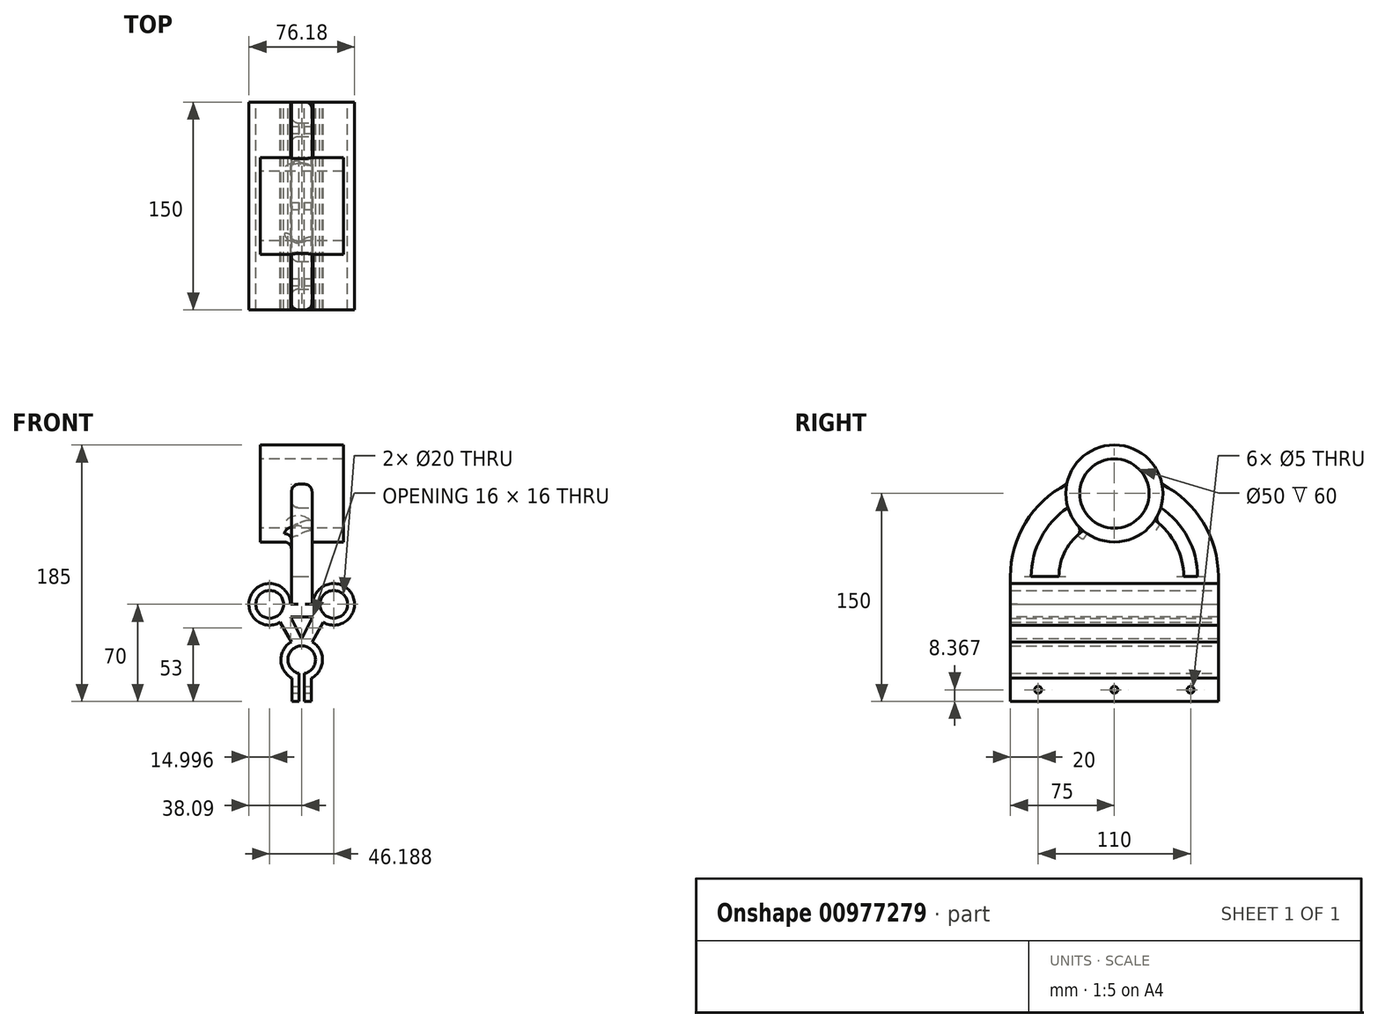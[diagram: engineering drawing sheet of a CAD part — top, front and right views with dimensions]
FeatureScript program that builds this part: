
annotation { "Feature Type Name" : "Feature", "Feature Type Description" : "" }
export const myFeature = defineFeature(function(context is Context, id is Id, definition is map)
    precondition{}
    {
        {
            var Q0;
            Q0=qCreatedBy(makeId("Front.planeOp"),FACE);
            var sketch = newSketch(context, id + "F0", { "sketchPlane" : qUnion([Q0])});
            skCircle(sketch, "E0", {"center": v(0, 0) * mm, "radius": 10 * mm});
            skCircle(sketch, "E1", {"center": v(23.1, 40) * mm, "radius": 10 * mm});
            skCircle(sketch, "E2", {"center": v(-23.1, 40) * mm, "radius": 10 * mm});
            skCircle(sketch, "E3", {"center": v(-23.1, 40) * mm, "radius": 15 * mm});
            skCircle(sketch, "E4", {"center": v(23.1, 40) * mm, "radius": 15 * mm});
            skCircle(sketch, "E5", {"center": v(0, 0) * mm, "radius": 15 * mm});
            skLineSegment(sketch, "E6", {"start": v(0, 0) * mm, "end": v(-23.1, 40) * mm});
            skLineSegment(sketch, "E7", {"start": v(23.1, 40) * mm, "end": v(0, 0) * mm});
            skLineSegment(sketch, "E8", {"start": v(-23.1, 40) * mm, "end": v(23.1, 40) * mm});
            skLineSegment(sketch, "E9.bottom", {"start": v(-2, 0) * mm, "end": v(2, 0) * mm});
            skLineSegment(sketch, "E9.top", {"start": v(-2, -30) * mm, "end": v(2, -30) * mm});
            skLineSegment(sketch, "E9.left", {"start": v(-2, 0) * mm, "end": v(-2, -30) * mm});
            skLineSegment(sketch, "E9.right", {"start": v(2, 0) * mm, "end": v(2, -30) * mm});
            skPoint(sketch, "E9.middle", {"position": v(0, -15) * mm});
            skLineSegment(sketch, "E10.bottom", {"start": v(7, -30) * mm, "end": v(-7, -30) * mm});
            skLineSegment(sketch, "E10.top", {"start": v(7, 0) * mm, "end": v(-7, 0) * mm});
            skLineSegment(sketch, "E10.left", {"start": v(7, -30) * mm, "end": v(7, 0) * mm});
            skLineSegment(sketch, "E10.right", {"start": v(-7, -30) * mm, "end": v(-7, 0) * mm});
            skLineSegment(sketch, "E11.bottom", {"start": v(-7.5, 60) * mm, "end": v(7.5, 60) * mm});
            skLineSegment(sketch, "E11.top", {"start": v(-7.5, 20) * mm, "end": v(7.5, 20) * mm});
            skLineSegment(sketch, "E11.left", {"start": v(-7.5, 60) * mm, "end": v(-7.5, 20) * mm});
            skLineSegment(sketch, "E11.right", {"start": v(7.5, 60) * mm, "end": v(7.5, 20) * mm});
            skPoint(sketch, "E11.middle", {"position": v(0, 40) * mm});
            skSolve(sketch);
        }
        {
            var Q0;
            {var subQ5=sQuery(id+"F0.wireOp",EDGE,"E11.bottom");Q0=makeQuery(id+"F0.imprint","IMPRINT",FACE,{"disambiguationData":[TD([[makeQuery(id+"F0.imprint","IMPRINT",EDGE,{"derivedFrom":subQ5}),-1.0]])]});}
            var Q1;
            {var subQ0=sQuery(id+"F0.wireOp",EDGE,"E7");var subQ1=sQuery(id+"F0.wireOp",EDGE,"E1");var subQ2=makeQuery(id+"F0.imprint","INTERSECT",VERTEX,{"derivedFrom":[subQ1,subQ0]});Q1=makeQuery(id+"F0.imprint","IMPRINT",FACE,{"disambiguationData":[TD([[makeQuery(id+"F0.imprint","IMPRINT",EDGE,{"disambiguationData":[TD([[subQ2,-1.0]])],"derivedFrom":subQ1}),-1.0]])]});}
            var Q2;
            {var subQ0=sQuery(id+"F0.wireOp",EDGE,"E6");var subQ1=sQuery(id+"F0.wireOp",EDGE,"E2");var subQ2=makeQuery(id+"F0.imprint","INTERSECT",VERTEX,{"derivedFrom":[subQ1,subQ0]});Q2=makeQuery(id+"F0.imprint","IMPRINT",FACE,{"disambiguationData":[TD([[makeQuery(id+"F0.imprint","IMPRINT",EDGE,{"disambiguationData":[TD([[subQ2,1.0]])],"derivedFrom":subQ1}),-1.0]])]});}
            var Q3;
            {var subQ0=sQuery(id+"F0.wireOp",EDGE,"E10.right");var subQ1=sQuery(id+"F0.wireOp",EDGE,"E5");var subQ2=makeQuery(id+"F0.imprint","INTERSECT",VERTEX,{"derivedFrom":[subQ1,subQ0]});Q3=makeQuery(id+"F0.imprint","IMPRINT",FACE,{"disambiguationData":[TD([[makeQuery(id+"F0.imprint","IMPRINT",EDGE,{"disambiguationData":[TD([[subQ2,-1.0]])],"derivedFrom":subQ1}),-1.0]])]});}
            var Q4;
            {var subQ0=sQuery(id+"F0.wireOp",EDGE,"E10.left");var subQ1=sQuery(id+"F0.wireOp",EDGE,"E5");var subQ2=makeQuery(id+"F0.imprint","INTERSECT",VERTEX,{"derivedFrom":[subQ1,subQ0]});Q4=makeQuery(id+"F0.imprint","IMPRINT",FACE,{"disambiguationData":[TD([[makeQuery(id+"F0.imprint","IMPRINT",EDGE,{"disambiguationData":[TD([[subQ2,1.0]])],"derivedFrom":subQ1}),-1.0]])]});}
            var Q5;
            {var subQ5=sQuery(id+"F0.wireOp",EDGE,"E11.top");Q5=makeQuery(id+"F0.imprint","IMPRINT",FACE,{"disambiguationData":[TD([[makeQuery(id+"F0.imprint","IMPRINT",EDGE,{"derivedFrom":subQ5}),1.0]])]});}
            var Q6;
            {var subQ0=sQuery(id+"F0.wireOp",EDGE,"E6");var subQ1=sQuery(id+"F0.wireOp",EDGE,"E0");var subQ2=makeQuery(id+"F0.imprint","INTERSECT",VERTEX,{"derivedFrom":[subQ1,subQ0]});Q6=makeQuery(id+"F0.imprint","IMPRINT",FACE,{"disambiguationData":[TD([[makeQuery(id+"F0.imprint","IMPRINT",EDGE,{"disambiguationData":[TD([[subQ2,-1.0]])],"derivedFrom":subQ1}),-1.0]])]});}
            var Q7;
            {var subQ0=sQuery(id+"F0.wireOp",EDGE,"E7");var subQ1=sQuery(id+"F0.wireOp",EDGE,"E0");var subQ2=makeQuery(id+"F0.imprint","INTERSECT",VERTEX,{"derivedFrom":[subQ1,subQ0]});Q7=makeQuery(id+"F0.imprint","IMPRINT",FACE,{"disambiguationData":[TD([[makeQuery(id+"F0.imprint","IMPRINT",EDGE,{"disambiguationData":[TD([[subQ2,1.0]])],"derivedFrom":subQ1}),-1.0]])]});}
            var Q8;
            {var subQ0=sQuery(id+"F0.wireOp",EDGE,"E7");var subQ1=sQuery(id+"F0.wireOp",EDGE,"E1");var subQ2=makeQuery(id+"F0.imprint","INTERSECT",VERTEX,{"derivedFrom":[subQ1,subQ0]});Q8=makeQuery(id+"F0.imprint","IMPRINT",FACE,{"disambiguationData":[TD([[makeQuery(id+"F0.imprint","IMPRINT",EDGE,{"disambiguationData":[TD([[subQ2,1.0]])],"derivedFrom":subQ1}),-1.0]])]});}
            var Q9;
            {var subQ0=sQuery(id+"F0.wireOp",EDGE,"E6");var subQ1=sQuery(id+"F0.wireOp",EDGE,"E2");var subQ2=makeQuery(id+"F0.imprint","INTERSECT",VERTEX,{"derivedFrom":[subQ1,subQ0]});Q9=makeQuery(id+"F0.imprint","IMPRINT",FACE,{"disambiguationData":[TD([[makeQuery(id+"F0.imprint","IMPRINT",EDGE,{"disambiguationData":[TD([[subQ2,-1.0]])],"derivedFrom":subQ1}),-1.0]])]});}
            var Q10;
            {var subQ0=sQuery(id+"F0.wireOp",EDGE,"E6");var subQ1=sQuery(id+"F0.wireOp",EDGE,"E0");var subQ2=makeQuery(id+"F0.imprint","INTERSECT",VERTEX,{"derivedFrom":[subQ1,subQ0]});Q10=makeQuery(id+"F0.imprint","IMPRINT",FACE,{"disambiguationData":[TD([[makeQuery(id+"F0.imprint","IMPRINT",EDGE,{"disambiguationData":[TD([[subQ2,1.0]])],"derivedFrom":subQ1}),-1.0]])]});}
            var Q11;
            {var subQ0=sQuery(id+"F0.wireOp",EDGE,"E10.right");var subQ1=sQuery(id+"F0.wireOp",EDGE,"E0");var subQ2=makeQuery(id+"F0.imprint","INTERSECT",VERTEX,{"derivedFrom":[subQ1,subQ0]});Q11=makeQuery(id+"F0.imprint","IMPRINT",FACE,{"disambiguationData":[TD([[makeQuery(id+"F0.imprint","IMPRINT",EDGE,{"disambiguationData":[TD([[subQ2,-1.0]])],"derivedFrom":subQ1}),-1.0]])]});}
            var Q12;
            {var subQ0=sQuery(id+"F0.wireOp",EDGE,"E9.right");var subQ1=sQuery(id+"F0.wireOp",EDGE,"E0");var subQ2=makeQuery(id+"F0.imprint","INTERSECT",VERTEX,{"derivedFrom":[subQ1,subQ0]});Q12=makeQuery(id+"F0.imprint","IMPRINT",FACE,{"disambiguationData":[TD([[makeQuery(id+"F0.imprint","IMPRINT",EDGE,{"disambiguationData":[TD([[subQ2,-1.0]])],"derivedFrom":subQ1}),-1.0]])]});}
            var Q13;
            {var subQ16=sQuery(id+"F0.wireOp",EDGE,"E11.top");Q13=makeQuery(id+"F0.imprint","IMPRINT",FACE,{"disambiguationData":[TD([[makeQuery(id+"F0.imprint","IMPRINT",EDGE,{"derivedFrom":subQ16}),-1.0]])]});}
            extrude(context, id + "F1", {"entities" : qUnion([Q0, Q1, Q2, Q3, Q4, Q5, Q6, Q7, Q8, Q9, Q10, Q11, Q12, Q13]), "depth" : 150 * mm, "offsetDistance" : 25 * mm});
        }
        {
            var Q0;
            Q0=makeQuery(id+"F1.opExtrude","SWEPT_FACE",FACE,{"disambiguationData":[OSD([sQuery(id+"F0.wireOp",EDGE,"E10.left")])]});
            var sketch = newSketch(context, id + "F2", { "sketchPlane" : qUnion([Q0])});
            skCircle(sketch, "E12", {"center": v(-130, -21.63) * mm, "radius": 2.5 * mm});
            skPoint(sketch, "E12.centerSnap0", {"position": v(-150, -21.63) * mm});
            skCircle(sketch, "E13", {"center": v(-75, -21.63) * mm, "radius": 2.5 * mm});
            skPoint(sketch, "E13.centerSnap0", {"position": v(-75, -30) * mm});
            skCircle(sketch, "E14", {"center": v(-20, -21.63) * mm, "radius": 2.5 * mm});
            skPoint(sketch, "E14.centerSnap0", {"position": v(0, -21.63) * mm});
            skSolve(sketch);
        }
        {
            var Q0;
            Q0=qSketchRegion(id+"F2",true);
            extrude(context, id + "F3", {"entities" : qUnion([Q0]), "operationType" : NewBodyOperationType.REMOVE, "oppositeDirection" : true, "depth" : 25 * mm, "offsetDistance" : 25 * mm});
        }
        {
            var Q0;
            Q0=qCreatedBy(makeId("Right.planeOp"),FACE);
            var sketch = newSketch(context, id + "F4", { "sketchPlane" : qUnion([Q0])});
            skArc(sketch, "E15", {"start": v(0, 60) * mm, "mid": v(-75, 135) * mm, "end": v(-150, 60) * mm});
            skCircle(sketch, "E16", {"center": v(-75, 120) * mm, "radius": 25 * mm});
            skCircle(sketch, "E17", {"center": v(-75, 120) * mm, "radius": 35 * mm});
            skLineSegment(sketch, "E18", {"start": v(0, 60) * mm, "end": v(-150, 60) * mm});
            skSolve(sketch);
        }
        {
            var Q0;
            Q0=qSketchRegion(id+"F4",true);
            var Q1;
            Q1=makeQuery(id+"F4.imprint","IMPRINT",FACE,{"disambiguationData":[TD([[makeQuery(id+"F4.imprint","IMPRINT",EDGE,{"derivedFrom":sQuery(id+"F4.wireOp",EDGE,"E16")}),-1.0]])]});
            extrude(context, id + "F5", {"entities" : qUnion([Q0, Q1]), "operationType" : NewBodyOperationType.ADD, "depth" : 15 * mm, "offsetDistance" : 25 * mm, "symmetric" : true});
        }
        {
            var Q0;
            Q0=makeQuery(id+"F4.imprint","IMPRINT",FACE,{"disambiguationData":[TD([[makeQuery(id+"F4.imprint","IMPRINT",EDGE,{"derivedFrom":sQuery(id+"F4.wireOp",EDGE,"E16")}),-1.0]])]});
            extrude(context, id + "F6", {"entities" : qUnion([Q0]), "operationType" : NewBodyOperationType.ADD, "depth" : 60 * mm, "offsetDistance" : 25 * mm, "symmetric" : true});
        }
        {
            var Q0;
            Q0=makeQuery(id+"F5.boolean.opBoolean","MERGE",FACE,{"derivedFrom":[makeQuery(id+"F1.opExtrude","SWEPT_FACE",FACE,{"disambiguationData":[OSD([sQuery(id+"F0.wireOp",EDGE,"E11.right")])]}),makeQuery(id+"F5.opExtrude","CAP_FACE",FACE,{"disambiguationData":[OSD([sQuery(id+"F4.wireOp",EDGE,"E15"),sQuery(id+"F4.wireOp",EDGE,"E16"),sQuery(id+"F4.wireOp",EDGE,"E18")])],"isStart":false})]});
            var sketch = newSketch(context, id + "F7", { "sketchPlane" : qUnion([Q0])});
            skCircle(sketch, "E19", {"center": v(-75, 60) * mm, "radius": 60 * mm});
            skCircle(sketch, "E20", {"center": v(-75, 60) * mm, "radius": 40 * mm});
            skLineSegment(sketch, "E21", {"start": v(-150, 60) * mm, "end": v(0, 60) * mm});
            skCircle(sketch, "E22", {"center": v(-75, 60) * mm, "radius": 50 * mm});
            skSolve(sketch);
        }
        {
            var Q0;
            {var subQ0=sQuery(id+"F7.wireOp",EDGE,"E21");var subQ1=sQuery(id+"F7.wireOp",EDGE,"E19");var subQ2=makeQuery(id+"F7.imprint","INTERSECT",VERTEX,{"disambiguationData":[OD(0.0)],"derivedFrom":[subQ1,subQ0]});Q0=makeQuery(id+"F7.imprint","IMPRINT",FACE,{"disambiguationData":[TD([[makeQuery(id+"F7.imprint","IMPRINT",EDGE,{"disambiguationData":[TD([[subQ2,1.0]])],"derivedFrom":subQ0}),1.0]])]});}
            var Q1;
            {var subQ0=sQuery(id+"F7.wireOp",EDGE,"E21");var subQ1=sQuery(id+"F7.wireOp",EDGE,"E19");var subQ2=makeQuery(id+"F7.imprint","INTERSECT",VERTEX,{"disambiguationData":[OD(1.0)],"derivedFrom":[subQ1,subQ0]});Q1=makeQuery(id+"F7.imprint","IMPRINT",FACE,{"disambiguationData":[TD([[makeQuery(id+"F7.imprint","IMPRINT",EDGE,{"disambiguationData":[TD([[subQ2,-1.0]])],"derivedFrom":subQ0}),1.0]])]});}
            var Q2;
            {var subQ0=sQuery(id+"F7.wireOp",EDGE,"E21");var subQ1=sQuery(id+"F7.wireOp",EDGE,"E20");var subQ2=makeQuery(id+"F7.imprint","INTERSECT",VERTEX,{"disambiguationData":[OD(0.0)],"derivedFrom":[subQ1,subQ0]});Q2=makeQuery(id+"F7.imprint","IMPRINT",FACE,{"disambiguationData":[TD([[makeQuery(id+"F7.imprint","IMPRINT",EDGE,{"disambiguationData":[TD([[subQ2,1.0]])],"derivedFrom":subQ0}),1.0]])]});}
            extrude(context, id + "F8", {"entities" : qUnion([Q0, Q1, Q2]), "operationType" : NewBodyOperationType.REMOVE, "oppositeDirection" : true, "depth" : 25 * mm, "offsetDistance" : 25 * mm});
        }
        {
            var Q0;
            Q0=makeQuery(id+"F1.opExtrude","CAP_FACE",FACE,{"disambiguationData":[OSD([sQuery(id+"F0.wireOp",EDGE,"E0"),sQuery(id+"F0.wireOp",EDGE,"E1"),sQuery(id+"F0.wireOp",EDGE,"E2"),sQuery(id+"F0.wireOp",EDGE,"E3"),sQuery(id+"F0.wireOp",EDGE,"E4"),sQuery(id+"F0.wireOp",EDGE,"E5"),sQuery(id+"F0.wireOp",EDGE,"E6"),sQuery(id+"F0.wireOp",EDGE,"E7"),sQuery(id+"F0.wireOp",EDGE,"E8"),sQuery(id+"F0.wireOp",EDGE,"E9.left"),sQuery(id+"F0.wireOp",EDGE,"E9.right"),sQuery(id+"F0.wireOp",EDGE,"E10.bottom"),sQuery(id+"F0.wireOp",EDGE,"E10.left"),sQuery(id+"F0.wireOp",EDGE,"E10.right"),sQuery(id+"F0.wireOp",EDGE,"E11.bottom"),sQuery(id+"F0.wireOp",EDGE,"E11.left"),sQuery(id+"F0.wireOp",EDGE,"E11.right")])],"isStart":false});
            var sketch = newSketch(context, id + "F9", { "sketchPlane" : qUnion([Q0])});
            skLineSegment(sketch, "E23", {"start": v(0, 15) * mm, "end": v(8, 31) * mm});
            skLineSegment(sketch, "E24", {"start": v(8, 31) * mm, "end": v(-8, 31) * mm});
            skLineSegment(sketch, "E25", {"start": v(-8, 31) * mm, "end": v(0, 15) * mm});
            skSolve(sketch);
        }
        {
            var Q0;
            Q0=makeQuery(id+"F9.imprint","IMPRINT",FACE,{"disambiguationData":[TD([[makeQuery(id+"F9.imprint","IMPRINT",EDGE,{"derivedFrom":sQuery(id+"F9.wireOp",EDGE,"E23")}),1.0]])]});
            extrude(context, id + "F10", {"entities" : qUnion([Q0]), "operationType" : NewBodyOperationType.REMOVE, "oppositeDirection" : true, "depth" : 400 * mm, "offsetDistance" : 25 * mm});
        }
        {
            var Q0;
            {var subQ0=sQuery(id+"F7.wireOp",EDGE,"E22");Q0=makeQuery(id+"F8.boolean.opBoolean","COPY",EDGE,{"derivedFrom":makeQuery(id+"F8.opExtrude","CAP_EDGE",EDGE,{"disambiguationData":[OSD([subQ0]),TDD([makeQuery(id+"F7.imprint","IMPRINT",EDGE,{"disambiguationData":[TD([[makeQuery(id+"F7.imprint","INTERSECT",VERTEX,{"disambiguationData":[OD(0.0)],"derivedFrom":[sQuery(id+"F7.wireOp",EDGE,"E21"),subQ0]}),1.0]])],"derivedFrom":subQ0})])],"isStart":true})});}
            var Q1;
            {var subQ0=sQuery(id+"F7.wireOp",EDGE,"E19");var subQ1=sQuery(id+"F4.wireOp",EDGE,"E17");var subQ2=sQuery(id+"F4.wireOp",EDGE,"E18");var subQ3=sQuery(id+"F4.wireOp",EDGE,"E16");var subQ4=sQuery(id+"F4.wireOp",EDGE,"E15");Q1=makeQuery(id+"F8.boolean.opBoolean","INTERSECT",EDGE,{"derivedFrom":[makeQuery(id+"F5.boolean.opBoolean","MERGE",FACE,{"derivedFrom":[makeQuery(id+"F1.opExtrude","SWEPT_FACE",FACE,{"disambiguationData":[OSD([sQuery(id+"F0.wireOp",EDGE,"E11.left")])]}),makeQuery(id+"F5.opExtrude","CAP_FACE",FACE,{"disambiguationData":[OSD([subQ4,subQ3,subQ1,subQ2])],"isStart":true})]}),makeQuery(id+"F8.opExtrude","SWEPT_FACE",FACE,{"disambiguationData":[OSD([subQ0]),TDD([makeQuery(id+"F7.imprint","IMPRINT",EDGE,{"disambiguationData":[TD([[makeQuery(id+"F7.imprint","INTERSECT",VERTEX,{"disambiguationData":[OD(1.0)],"derivedFrom":[subQ0,sQuery(id+"F7.wireOp",EDGE,"E21")]}),1.0]])],"derivedFrom":subQ0})])]})]});}
            var Q2;
            {var subQ0=sQuery(id+"F7.wireOp",EDGE,"E22");Q2=makeQuery(id+"F8.boolean.opBoolean","COPY",EDGE,{"derivedFrom":makeQuery(id+"F8.opExtrude","CAP_EDGE",EDGE,{"disambiguationData":[OSD([subQ0]),TDD([makeQuery(id+"F7.imprint","IMPRINT",EDGE,{"disambiguationData":[TD([[makeQuery(id+"F7.imprint","INTERSECT",VERTEX,{"disambiguationData":[OD(1.0)],"derivedFrom":[sQuery(id+"F7.wireOp",EDGE,"E21"),subQ0]}),-1.0]])],"derivedFrom":subQ0})])],"isStart":true})});}
            var Q3;
            {var subQ0=sQuery(id+"F7.wireOp",EDGE,"E19");Q3=makeQuery(id+"F8.boolean.opBoolean","COPY",EDGE,{"derivedFrom":makeQuery(id+"F8.opExtrude","CAP_EDGE",EDGE,{"disambiguationData":[OSD([subQ0]),TDD([makeQuery(id+"F7.imprint","IMPRINT",EDGE,{"disambiguationData":[TD([[makeQuery(id+"F7.imprint","INTERSECT",VERTEX,{"disambiguationData":[OD(0.0)],"derivedFrom":[subQ0,sQuery(id+"F7.wireOp",EDGE,"E21")]}),-1.0]])],"derivedFrom":subQ0})])],"isStart":true})});}
            var Q4;
            {var subQ0=sQuery(id+"F4.wireOp",EDGE,"E15");Q4=makeQuery(id+"F5.opExtrude","CAP_EDGE",EDGE,{"disambiguationData":[OSD([subQ0]),TDD([makeQuery(id+"F4.imprint","IMPRINT",EDGE,{"disambiguationData":[TD([[makeQuery(id+"F4.imprint","INTERSECT",VERTEX,{"disambiguationData":[OD(0.0)],"derivedFrom":[subQ0,sQuery(id+"F4.wireOp",EDGE,"E18")]}),-1.0]])],"derivedFrom":subQ0})])],"isStart":false});}
            var Q5;
            {var subQ0=sQuery(id+"F4.wireOp",EDGE,"E15");Q5=makeQuery(id+"F5.opExtrude","CAP_EDGE",EDGE,{"disambiguationData":[OSD([subQ0]),TDD([makeQuery(id+"F4.imprint","IMPRINT",EDGE,{"disambiguationData":[TD([[makeQuery(id+"F4.imprint","INTERSECT",VERTEX,{"disambiguationData":[OD(1.0)],"derivedFrom":[subQ0,sQuery(id+"F4.wireOp",EDGE,"E18")]}),1.0]])],"derivedFrom":subQ0})])],"isStart":false});}
            var Q6;
            {var subQ0=sQuery(id+"F7.wireOp",EDGE,"E20");var subQ1=sQuery(id+"F4.wireOp",EDGE,"E17");var subQ2=sQuery(id+"F4.wireOp",EDGE,"E18");var subQ3=sQuery(id+"F4.wireOp",EDGE,"E16");var subQ4=sQuery(id+"F4.wireOp",EDGE,"E15");Q6=makeQuery(id+"F8.boolean.opBoolean","INTERSECT",EDGE,{"derivedFrom":[makeQuery(id+"F5.boolean.opBoolean","MERGE",FACE,{"derivedFrom":[makeQuery(id+"F1.opExtrude","SWEPT_FACE",FACE,{"disambiguationData":[OSD([sQuery(id+"F0.wireOp",EDGE,"E11.left")])]}),makeQuery(id+"F5.opExtrude","CAP_FACE",FACE,{"disambiguationData":[OSD([subQ4,subQ3,subQ1,subQ2])],"isStart":true})]}),makeQuery(id+"F8.opExtrude","SWEPT_FACE",FACE,{"disambiguationData":[OSD([subQ0]),TDD([makeQuery(id+"F7.imprint","IMPRINT",EDGE,{"disambiguationData":[TD([[makeQuery(id+"F7.imprint","INTERSECT",VERTEX,{"disambiguationData":[OD(1.0)],"derivedFrom":[subQ0,sQuery(id+"F7.wireOp",EDGE,"E21")]}),1.0]])],"derivedFrom":subQ0})])]})]});}
            var Q7;
            {var subQ0=sQuery(id+"F7.wireOp",EDGE,"E20");Q7=makeQuery(id+"F8.boolean.opBoolean","COPY",EDGE,{"derivedFrom":makeQuery(id+"F8.opExtrude","CAP_EDGE",EDGE,{"disambiguationData":[OSD([subQ0]),TDD([makeQuery(id+"F7.imprint","IMPRINT",EDGE,{"disambiguationData":[TD([[makeQuery(id+"F7.imprint","INTERSECT",VERTEX,{"disambiguationData":[OD(0.0)],"derivedFrom":[subQ0,sQuery(id+"F7.wireOp",EDGE,"E21")]}),-1.0]])],"derivedFrom":subQ0})])],"isStart":true})});}
            var Q8;
            {var subQ0=sQuery(id+"F7.wireOp",EDGE,"E20");var subQ1=sQuery(id+"F4.wireOp",EDGE,"E17");var subQ2=sQuery(id+"F4.wireOp",EDGE,"E18");var subQ3=sQuery(id+"F4.wireOp",EDGE,"E16");var subQ4=sQuery(id+"F4.wireOp",EDGE,"E15");Q8=makeQuery(id+"F8.boolean.opBoolean","INTERSECT",EDGE,{"derivedFrom":[makeQuery(id+"F5.boolean.opBoolean","MERGE",FACE,{"derivedFrom":[makeQuery(id+"F1.opExtrude","SWEPT_FACE",FACE,{"disambiguationData":[OSD([sQuery(id+"F0.wireOp",EDGE,"E11.left")])]}),makeQuery(id+"F5.opExtrude","CAP_FACE",FACE,{"disambiguationData":[OSD([subQ4,subQ3,subQ1,subQ2])],"isStart":true})]}),makeQuery(id+"F8.opExtrude","SWEPT_FACE",FACE,{"disambiguationData":[OSD([subQ0]),TDD([makeQuery(id+"F7.imprint","IMPRINT",EDGE,{"disambiguationData":[TD([[makeQuery(id+"F7.imprint","INTERSECT",VERTEX,{"disambiguationData":[OD(0.0)],"derivedFrom":[subQ0,sQuery(id+"F7.wireOp",EDGE,"E21")]}),-1.0]])],"derivedFrom":subQ0})])]})]});}
            var Q9;
            {var subQ0=sQuery(id+"F7.wireOp",EDGE,"E22");var subQ1=sQuery(id+"F4.wireOp",EDGE,"E17");var subQ2=sQuery(id+"F4.wireOp",EDGE,"E18");var subQ3=sQuery(id+"F4.wireOp",EDGE,"E16");var subQ4=sQuery(id+"F4.wireOp",EDGE,"E15");Q9=makeQuery(id+"F8.boolean.opBoolean","INTERSECT",EDGE,{"derivedFrom":[makeQuery(id+"F5.boolean.opBoolean","MERGE",FACE,{"derivedFrom":[makeQuery(id+"F1.opExtrude","SWEPT_FACE",FACE,{"disambiguationData":[OSD([sQuery(id+"F0.wireOp",EDGE,"E11.left")])]}),makeQuery(id+"F5.opExtrude","CAP_FACE",FACE,{"disambiguationData":[OSD([subQ4,subQ3,subQ1,subQ2])],"isStart":true})]}),makeQuery(id+"F8.opExtrude","SWEPT_FACE",FACE,{"disambiguationData":[OSD([subQ0]),TDD([makeQuery(id+"F7.imprint","IMPRINT",EDGE,{"disambiguationData":[TD([[makeQuery(id+"F7.imprint","INTERSECT",VERTEX,{"disambiguationData":[OD(1.0)],"derivedFrom":[sQuery(id+"F7.wireOp",EDGE,"E21"),subQ0]}),-1.0]])],"derivedFrom":subQ0})])]})]});}
            var Q10;
            {var subQ0=sQuery(id+"F7.wireOp",EDGE,"E19");var subQ1=sQuery(id+"F4.wireOp",EDGE,"E17");var subQ2=sQuery(id+"F4.wireOp",EDGE,"E18");var subQ3=sQuery(id+"F4.wireOp",EDGE,"E16");var subQ4=sQuery(id+"F4.wireOp",EDGE,"E15");Q10=makeQuery(id+"F8.boolean.opBoolean","INTERSECT",EDGE,{"derivedFrom":[makeQuery(id+"F5.boolean.opBoolean","MERGE",FACE,{"derivedFrom":[makeQuery(id+"F1.opExtrude","SWEPT_FACE",FACE,{"disambiguationData":[OSD([sQuery(id+"F0.wireOp",EDGE,"E11.left")])]}),makeQuery(id+"F5.opExtrude","CAP_FACE",FACE,{"disambiguationData":[OSD([subQ4,subQ3,subQ1,subQ2])],"isStart":true})]}),makeQuery(id+"F8.opExtrude","SWEPT_FACE",FACE,{"disambiguationData":[OSD([subQ0]),TDD([makeQuery(id+"F7.imprint","IMPRINT",EDGE,{"disambiguationData":[TD([[makeQuery(id+"F7.imprint","INTERSECT",VERTEX,{"disambiguationData":[OD(0.0)],"derivedFrom":[subQ0,sQuery(id+"F7.wireOp",EDGE,"E21")]}),-1.0]])],"derivedFrom":subQ0})])]})]});}
            var Q11;
            {var subQ0=sQuery(id+"F4.wireOp",EDGE,"E17");var subQ1=sQuery(id+"F4.wireOp",EDGE,"E15");Q11=makeQuery(id+"F5.opExtrude","SWEPT_EDGE",EDGE,{"disambiguationData":[OSD([subQ1,subQ0]),TDD([makeQuery(id+"F4.imprint","INTERSECT",VERTEX,{"disambiguationData":[OD(0.0)],"derivedFrom":[subQ1,subQ0]})])]});}
            var Q12;
            {var subQ0=sQuery(id+"F4.wireOp",EDGE,"E15");Q12=makeQuery(id+"F5.opExtrude","CAP_EDGE",EDGE,{"disambiguationData":[OSD([subQ0]),TDD([makeQuery(id+"F4.imprint","IMPRINT",EDGE,{"disambiguationData":[TD([[makeQuery(id+"F4.imprint","INTERSECT",VERTEX,{"disambiguationData":[OD(1.0)],"derivedFrom":[subQ0,sQuery(id+"F4.wireOp",EDGE,"E18")]}),1.0]])],"derivedFrom":subQ0})])],"isStart":true});}
            var Q13;
            {var subQ0=sQuery(id+"F4.wireOp",EDGE,"E17");var subQ1=sQuery(id+"F4.wireOp",EDGE,"E15");Q13=makeQuery(id+"F5.opExtrude","SWEPT_EDGE",EDGE,{"disambiguationData":[OSD([subQ1,subQ0]),TDD([makeQuery(id+"F4.imprint","INTERSECT",VERTEX,{"disambiguationData":[OD(1.0)],"derivedFrom":[subQ1,subQ0]})])]});}
            var Q14;
            {var subQ0=sQuery(id+"F7.wireOp",EDGE,"E22");var subQ1=sQuery(id+"F4.wireOp",EDGE,"E17");var subQ2=sQuery(id+"F4.wireOp",EDGE,"E18");var subQ3=sQuery(id+"F4.wireOp",EDGE,"E16");var subQ4=sQuery(id+"F4.wireOp",EDGE,"E15");Q14=makeQuery(id+"F8.boolean.opBoolean","INTERSECT",EDGE,{"derivedFrom":[makeQuery(id+"F5.boolean.opBoolean","MERGE",FACE,{"derivedFrom":[makeQuery(id+"F1.opExtrude","SWEPT_FACE",FACE,{"disambiguationData":[OSD([sQuery(id+"F0.wireOp",EDGE,"E11.left")])]}),makeQuery(id+"F5.opExtrude","CAP_FACE",FACE,{"disambiguationData":[OSD([subQ4,subQ3,subQ1,subQ2])],"isStart":true})]}),makeQuery(id+"F8.opExtrude","SWEPT_FACE",FACE,{"disambiguationData":[OSD([subQ0]),TDD([makeQuery(id+"F7.imprint","IMPRINT",EDGE,{"disambiguationData":[TD([[makeQuery(id+"F7.imprint","INTERSECT",VERTEX,{"disambiguationData":[OD(0.0)],"derivedFrom":[sQuery(id+"F7.wireOp",EDGE,"E21"),subQ0]}),1.0]])],"derivedFrom":subQ0})])]})]});}
            var Q15;
            {var subQ0=sQuery(id+"F4.wireOp",EDGE,"E17");var subQ1=makeQuery(id+"F6.opExtrude","SWEPT_FACE",FACE,{"disambiguationData":[OSD([subQ0])]});var subQ2=sQuery(id+"F7.wireOp",EDGE,"E21");var subQ3=sQuery(id+"F7.wireOp",EDGE,"E20");var subQ4=sQuery(id+"F4.wireOp",EDGE,"E18");var subQ5=sQuery(id+"F4.wireOp",EDGE,"E16");var subQ6=sQuery(id+"F4.wireOp",EDGE,"E15");var subQ12=makeQuery(id+"F5.opExtrude","CAP_FACE",FACE,{"disambiguationData":[OSD([subQ6,subQ5,subQ0,subQ4])],"isStart":true});var subQ13=makeQuery(id+"F1.opExtrude","SWEPT_FACE",FACE,{"disambiguationData":[OSD([sQuery(id+"F0.wireOp",EDGE,"E11.left")])]});Q15=makeQuery(id+"F8.boolean.opBoolean","SPLIT",EDGE,{"disambiguationData":[TD([makeQuery(id+"F8.opExtrude","SWEPT_FACE",FACE,{"disambiguationData":[OSD([subQ3]),TDD([makeQuery(id+"F7.imprint","IMPRINT",EDGE,{"disambiguationData":[TD([[makeQuery(id+"F7.imprint","INTERSECT",VERTEX,{"disambiguationData":[OD(1.0)],"derivedFrom":[subQ3,subQ2]}),1.0]])],"derivedFrom":subQ3})])]})])],"derivedFrom":makeQuery(id+"F6.boolean.opBoolean","INTERSECT",EDGE,{"derivedFrom":[makeQuery(id+"F5.boolean.opBoolean","MERGE",FACE,{"derivedFrom":[subQ13,subQ12]}),subQ1]})});}
            var Q16;
            {var subQ0=sQuery(id+"F4.wireOp",EDGE,"E17");var subQ1=makeQuery(id+"F6.opExtrude","SWEPT_FACE",FACE,{"disambiguationData":[OSD([subQ0])]});var subQ2=sQuery(id+"F4.wireOp",EDGE,"E18");var subQ3=sQuery(id+"F4.wireOp",EDGE,"E16");var subQ4=sQuery(id+"F4.wireOp",EDGE,"E15");var subQ5=makeQuery(id+"F5.opExtrude","CAP_FACE",FACE,{"disambiguationData":[OSD([subQ4,subQ3,subQ0,subQ2])],"isStart":true});var subQ6=makeQuery(id+"F1.opExtrude","SWEPT_FACE",FACE,{"disambiguationData":[OSD([sQuery(id+"F0.wireOp",EDGE,"E11.left")])]});var subQ12=sQuery(id+"F7.wireOp",EDGE,"E21");var subQ13=sQuery(id+"F7.wireOp",EDGE,"E20");Q16=makeQuery(id+"F8.boolean.opBoolean","SPLIT",EDGE,{"disambiguationData":[TD([makeQuery(id+"F8.opExtrude","SWEPT_FACE",FACE,{"disambiguationData":[OSD([subQ13]),TDD([makeQuery(id+"F7.imprint","IMPRINT",EDGE,{"disambiguationData":[TD([[makeQuery(id+"F7.imprint","INTERSECT",VERTEX,{"disambiguationData":[OD(0.0)],"derivedFrom":[subQ13,subQ12]}),-1.0]])],"derivedFrom":subQ13})])]})])],"derivedFrom":makeQuery(id+"F6.boolean.opBoolean","INTERSECT",EDGE,{"derivedFrom":[makeQuery(id+"F5.boolean.opBoolean","MERGE",FACE,{"derivedFrom":[subQ6,subQ5]}),subQ1]})});}
            fillet(context, id + "F11", {"entities" : qUnion([Q0, Q1, Q2, Q3, Q4, Q5, Q6, Q7, Q8, Q9, Q10, Q11, Q12, Q13, Q14, Q15, Q16]), "radius" : 5 * mm, "tangentPropagation" : true, "allowEdgeOverflow" : false});
        }
    });
